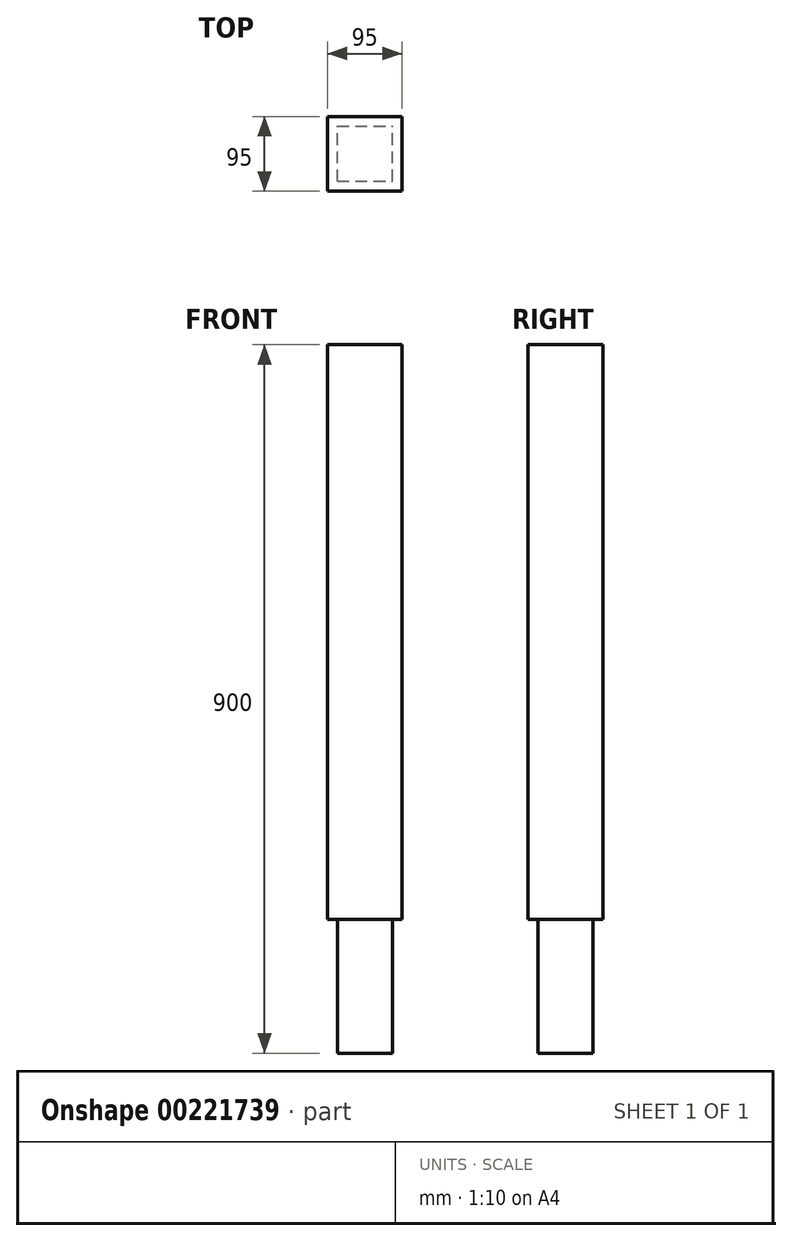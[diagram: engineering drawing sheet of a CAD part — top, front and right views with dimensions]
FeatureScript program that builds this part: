
annotation { "Feature Type Name" : "Feature", "Feature Type Description" : "" }
export const myFeature = defineFeature(function(context is Context, id is Id, definition is map)
    precondition{}
    {
        {
            var Q0;
            Q0=qCreatedBy(makeId("Top.planeOp"),FACE);
            var sketch = newSketch(context, id + "F0", { "sketchPlane" : qUnion([Q0])});
            skLineSegment(sketch, "E0.bottom", {"start": v(-47.5, 47.5) * mm, "end": v(47.5, 47.5) * mm});
            skLineSegment(sketch, "E0.top", {"start": v(-47.5, -47.5) * mm, "end": v(47.5, -47.5) * mm});
            skLineSegment(sketch, "E0.left", {"start": v(-47.5, 47.5) * mm, "end": v(-47.5, -47.5) * mm});
            skLineSegment(sketch, "E0.right", {"start": v(47.5, 47.5) * mm, "end": v(47.5, -47.5) * mm});
            skPoint(sketch, "E0.middle", {"position": v(0, 0) * mm});
            skSolve(sketch);
        }
        {
            var Q0;
            Q0 = qSketchRegion(id + "F0", true);
            extrude(context, id + "F1", {"entities" : qUnion([Q0]), "oppositeDirection" : true, "depth" : 900 * mm});
        }
        {
            var Q0;
            Q0=makeQuery(id+"F1.opExtrude","CAP_FACE",FACE,{"disambiguationData":[OSD([sQuery(id+"F0.wireOp",EDGE,"E0.bottom"),sQuery(id+"F0.wireOp",EDGE,"E0.top"),sQuery(id+"F0.wireOp",EDGE,"E0.left"),sQuery(id+"F0.wireOp",EDGE,"E0.right")])],"isStart":false});
            var sketch = newSketch(context, id + "F2", { "sketchPlane" : qUnion([Q0])});
            skLineSegment(sketch, "E1.0.0", {"start": v(-47.5, 47.5) * mm, "end": v(-47.5, -47.5) * mm});
            skLineSegment(sketch, "E1.0.1", {"start": v(-47.5, -47.5) * mm, "end": v(47.5, -47.5) * mm});
            skLineSegment(sketch, "E1.0.2", {"start": v(47.5, -47.5) * mm, "end": v(47.5, 47.5) * mm});
            skLineSegment(sketch, "E1.0.3", {"start": v(47.5, 47.5) * mm, "end": v(-47.5, 47.5) * mm});
            skLineSegment(sketch, "E2.bottom", {"start": v(-35, 35) * mm, "end": v(35, 35) * mm});
            skLineSegment(sketch, "E2.top", {"start": v(-35, -35) * mm, "end": v(35, -35) * mm});
            skLineSegment(sketch, "E2.left", {"start": v(-35, 35) * mm, "end": v(-35, -35) * mm});
            skLineSegment(sketch, "E2.right", {"start": v(35, 35) * mm, "end": v(35, -35) * mm});
            skPoint(sketch, "E2.middle", {"position": v(0, 0) * mm});
            skSolve(sketch);
        }
        {
            var Q0;
            Q0 = qSketchRegion(id + "F2", true);
            extrude(context, id + "F3", {"entities" : qUnion([Q0]), "operationType" : NewBodyOperationType.REMOVE, "oppositeDirection" : true, "depth" : 170 * mm});
        }
    });
